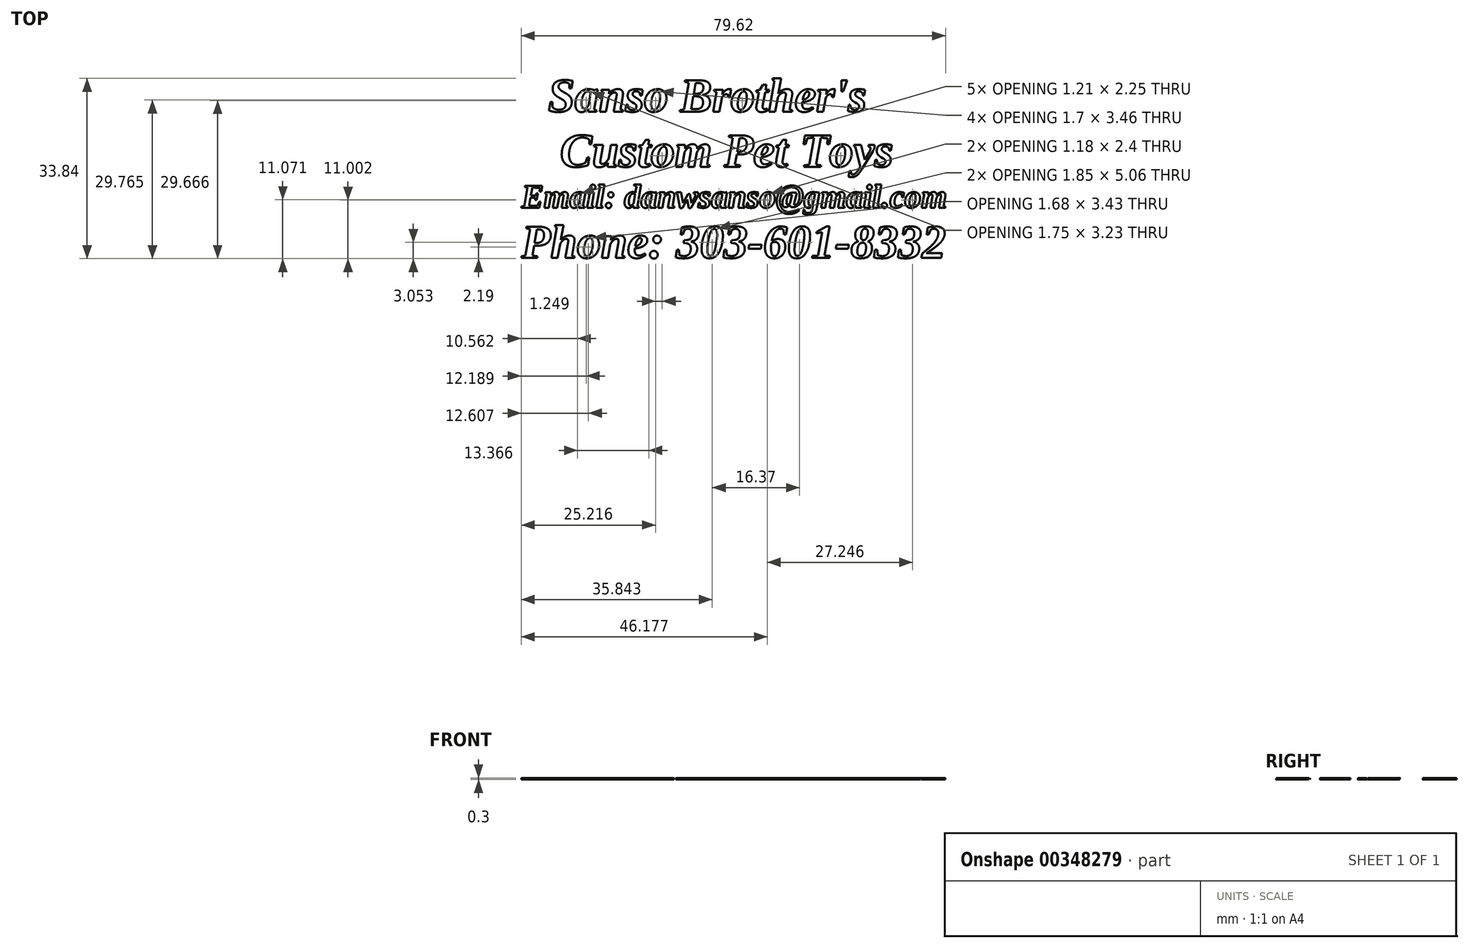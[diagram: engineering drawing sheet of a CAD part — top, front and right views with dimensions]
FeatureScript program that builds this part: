
annotation { "Feature Type Name" : "Feature", "Feature Type Description" : "" }
export const myFeature = defineFeature(function(context is Context, id is Id, definition is map)
    precondition{}
    {
        {
            var Q0;
            Q0=qCreatedBy(makeId("Top.planeOp"),FACE);
            var sketch = newSketch(context, id + "F0", { "sketchPlane" : qUnion([Q0])});
            skText(sketch, "E0", { "text": "Sanso Brother\'s\n Custom Pet Toys", "fontName": "Tinos-BoldItalic.ttf"});
            skText(sketch, "E1", { "text": "Email: <email>", "fontName": "Tinos-BoldItalic.ttf"});
            skText(sketch, "E2", { "text": "Phone: 303-601-8332", "fontName": "Tinos-BoldItalic.ttf"});
            const initialGuessF0  = {"E0": [-0.05156, -0.06174, 1, 0, 0.00648], "E1": [-0.05656, -0.07977, 1, 0, 0.0045], "E2": [-0.05656, -0.0892, 1, 0, 0.00643]};
            skSetInitialGuess(sketch, initialGuessF0);
            skSolve(sketch);
        }
        {
            var Q0;
            Q0 = qSketchRegion(id + "F0", true);
            extrude(context, id + "F1", {"entities" : qUnion([Q0]), "depth" : .3 * mm, "offsetDistance" : 25 * mm});
        }
    });
